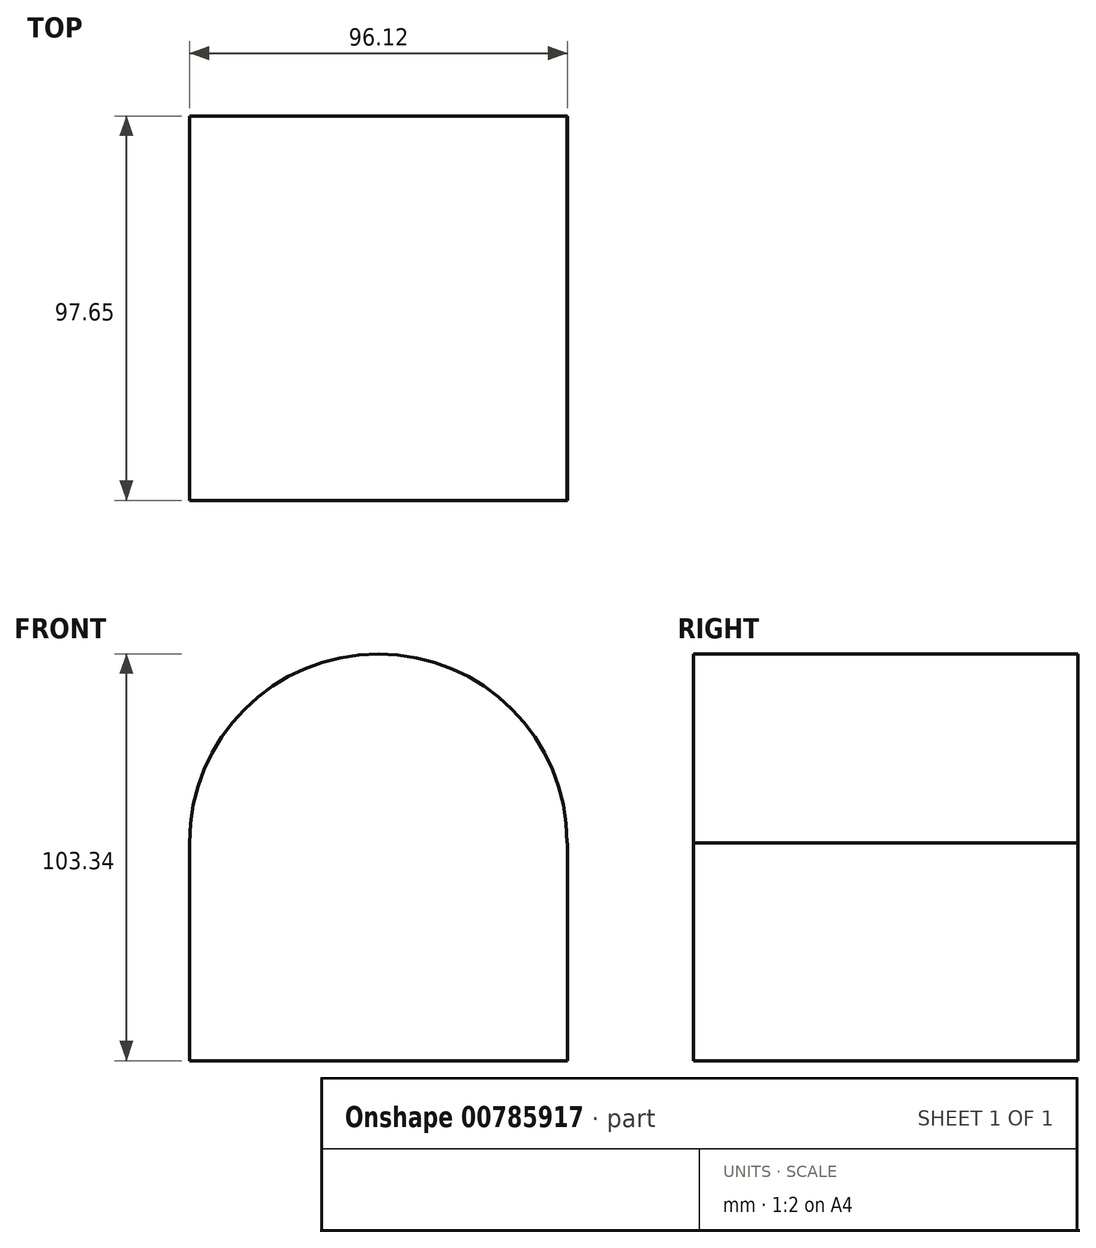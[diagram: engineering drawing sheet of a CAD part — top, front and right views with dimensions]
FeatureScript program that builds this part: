
annotation { "Feature Type Name" : "Feature", "Feature Type Description" : "" }
export const myFeature = defineFeature(function(context is Context, id is Id, definition is map)
    precondition{}
    {
        {
            var Q0;
            Q0=qCreatedBy(makeId("Front.planeOp"),FACE);
            var sketch = newSketch(context, id + "F0", { "sketchPlane" : qUnion([Q0])});
            skArc(sketch, "E0", {"start": v(-48, 0) * mm, "mid": v(0, 48) * mm, "end": v(48, 0) * mm});
            skLineSegment(sketch, "E1", {"start": v(-48, 0) * mm, "end": v(48, 0) * mm});
            skLineSegment(sketch, "E2.bottom", {"start": v(-48, 0) * mm, "end": v(48.13, 0) * mm});
            skLineSegment(sketch, "E2.top", {"start": v(-48, -55.35) * mm, "end": v(48.13, -55.35) * mm});
            skLineSegment(sketch, "E2.left", {"start": v(-48, 0) * mm, "end": v(-48, -55.35) * mm});
            skLineSegment(sketch, "E2.right", {"start": v(48.13, 0) * mm, "end": v(48.13, -55.35) * mm});
            skArc(sketch, "E3", {"start": v(48.13, -55.35) * mm, "mid": v(0.13, -103.48) * mm, "end": v(-48.18, -55.68) * mm});
            skSolve(sketch);
        }
        {
            var Q0;
            Q0=makeQuery(id+"F0.imprint","IMPRINT",FACE,{"disambiguationData":[TD([[makeQuery(id+"F0.imprint","IMPRINT",EDGE,{"derivedFrom":sQuery(id+"F0.wireOp",EDGE,"E2.top")}),1.0]])]});
            var Q1;
            {var subQ0=sQuery(id+"F0.wireOp",EDGE,"E0");Q1=makeQuery(id+"F0.imprint","IMPRINT",FACE,{"disambiguationData":[TD([[makeQuery(id+"F0.imprint","IMPRINT",EDGE,{"derivedFrom":subQ0}),-1.0]])]});}
            var Q2;
            Q2 = qSketchRegion(id + "F0", true);
            extrude(context, id + "F1", {"entities" : qUnion([Q0, Q1, Q2]), "depth" : 97.65 * mm, "offsetDistance" : 25.4 * mm});
        }
        {
            var Q0;
            Q0=sQuery(id+"F0.wireOp",EDGE,"E3");
            extrude(context, id + "F2", {"bodyType" : ToolBodyType.SURFACE, "surfaceEntities" : qUnion([Q0]), "depth" : 127 * mm, "offsetDistance" : 25.4 * mm});
        }
    });
